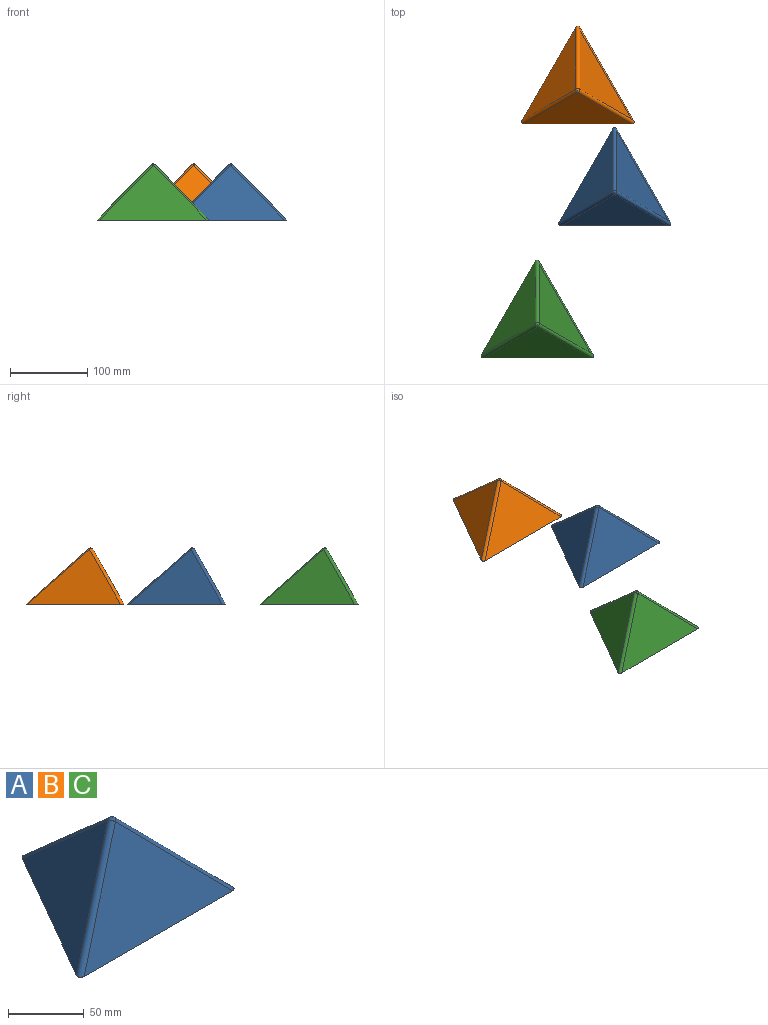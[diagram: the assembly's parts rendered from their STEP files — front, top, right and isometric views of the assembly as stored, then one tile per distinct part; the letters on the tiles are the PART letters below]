
ASSEMBLY  parts=3 mates=2
PART A: 17 faces, bbox 145.8x127x73.5 mm
  f0: plane 145.09x126.47mm, normal (0,0,-1), area 9626.1mm2, adj f1,f2,f3,f4,f5,f7
  f1: plane 120.09x70.81mm, normal (-0.75,0.44,0.49), area 5639.9mm2, adj f0,f4,f5
  f2: plane 138.67x70.81mm, normal (0,-0.87,0.49), area 5639.9mm2, adj f0,f4,f7
  f3: plane 120.09x69.34mm, normal (0.75,0.44,0.49), area 494.4mm2, adj f0,f5,f7,f10
  f4: cylinder r=3.5mm len=72.88mm, axis (0.65,0.37,0.66), area 644.3mm2, adj f0,f1,f2,f6
  f5: cylinder r=3.5mm len=81.88mm, axis (0,-0.75,0.66), area 644.3mm2, adj f0,f1,f3,f6,f9
  f6: sphere r=3.5mm, area 25.1mm2, adj f4,f5,f7
  f7: cylinder r=3.5mm len=72.88mm, axis (-0.65,0.37,0.66), area 644.3mm2, adj f0,f2,f3,f6,f8
  f8: plane 68.62x67.64mm, normal (-0.1,0.82,-0.56), area 320.4mm2, adj f7,f9,f10,f16
  f9: plane 77.85x67.64mm, normal (0.66,-0.5,-0.56), area 320.4mm2, adj f5,f8,f10,f14
  f10: plane 133.86x115.63mm, normal (0,0,1), area 7837.3mm2, adj f3,f8,f9,f11,f12,f13,f14,f16
  f11: plane 112.06x66.07mm, normal (0.75,-0.44,-0.49), area 4910.5mm2, adj f10,f13,f14
  f12: plane 129.39x66.07mm, normal (0,0.87,-0.49), area 4910.5mm2, adj f10,f13,f16
  f13: cylinder r=0.33mm len=66.24mm, axis (0.65,0.37,0.66), area 55.4mm2, adj f10,f11,f12,f15
  f14: cylinder r=0.33mm len=74.87mm, axis (0,-0.75,0.66), area 55.4mm2, adj f9,f10,f11,f15
  f15: sphere r=0.33mm, area 0.2mm2, adj f13,f14,f16
  f16: cylinder r=0.33mm len=66.24mm, axis (-0.65,0.37,0.66), area 55.4mm2, adj f8,f10,f12,f15
PART B: same geometry as A
PART C: same geometry as A
PLACE A t=(145.23,8.89,33.4)mm
PLACE B t=(97.56,140.09,33.4)mm
PLACE C t=(45.16,-162.1,33.4)mm
MATE planar B.f0 <-> C.f0  axis (0,0,-1) through (97.56,140.09,33.4)mm
MATE planar B.f0 <-> A.f0  axis (0,0,-1) through (97.56,140.09,33.4)mm
